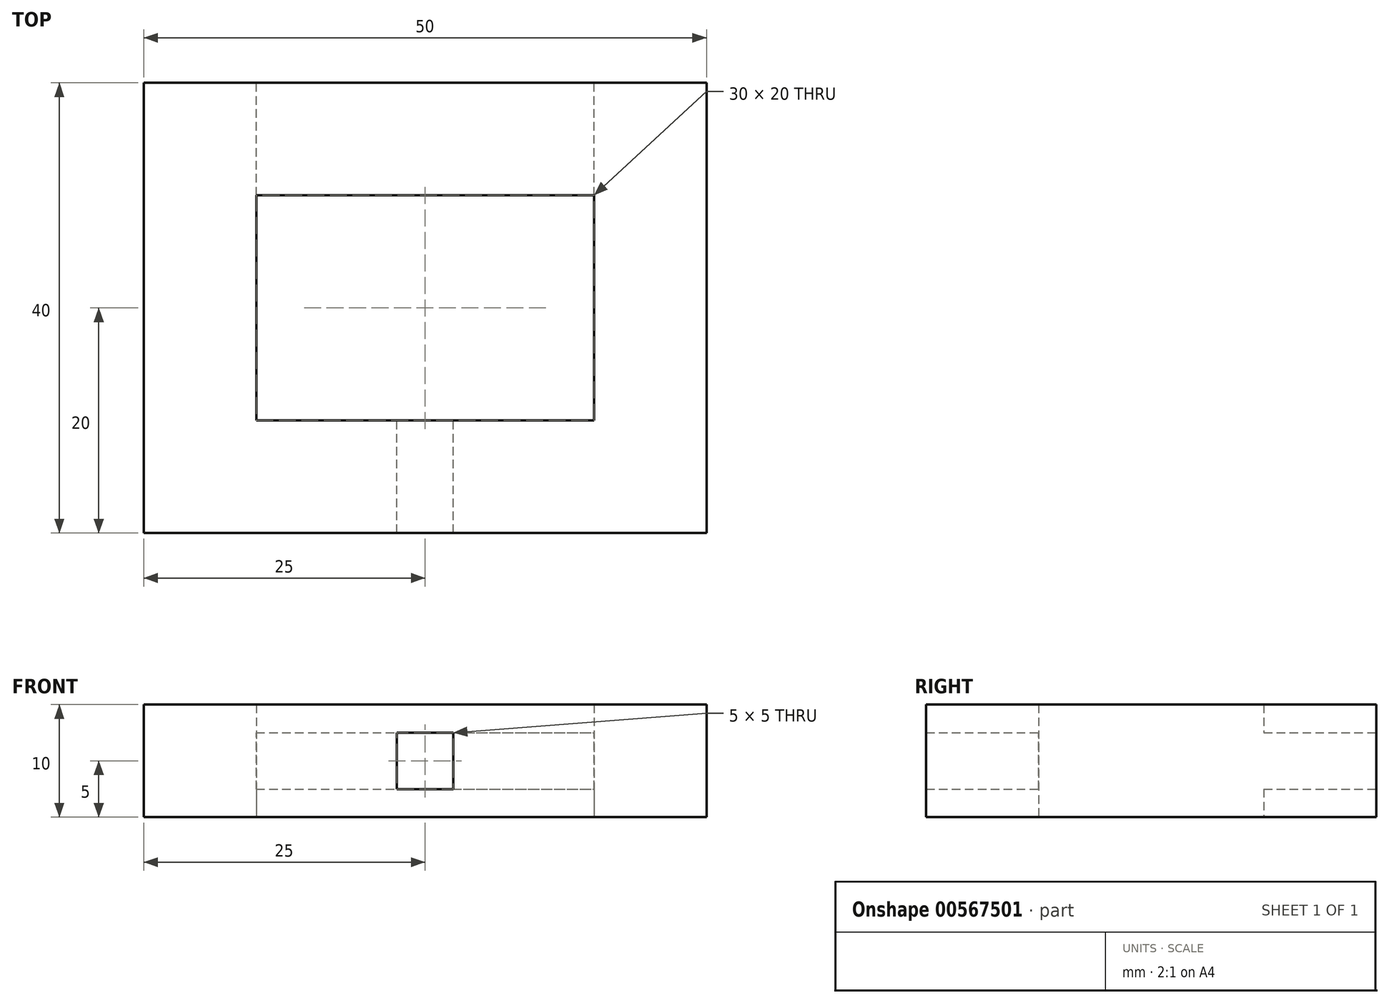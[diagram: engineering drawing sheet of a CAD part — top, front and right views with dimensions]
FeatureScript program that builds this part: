
annotation { "Feature Type Name" : "Feature", "Feature Type Description" : "" }
export const myFeature = defineFeature(function(context is Context, id is Id, definition is map)
    precondition{}
    {
        {
            var Q0;
            Q0=qCreatedBy(makeId("Top.planeOp"),FACE);
            var sketch = newSketch(context, id + "F0", { "sketchPlane" : qUnion([Q0])});
            skLineSegment(sketch, "E0.bottom", {"start": v(-25, 20) * mm, "end": v(25, 20) * mm});
            skLineSegment(sketch, "E0.top", {"start": v(-25, -20) * mm, "end": v(25, -20) * mm});
            skLineSegment(sketch, "E0.left", {"start": v(-25, 20) * mm, "end": v(-25, -20) * mm});
            skLineSegment(sketch, "E0.right", {"start": v(25, 20) * mm, "end": v(25, -20) * mm});
            skPoint(sketch, "E0.middle", {"position": v(0, 0) * mm});
            skLineSegment(sketch, "E1.0", {"start": v(15, 10) * mm, "end": v(15, -10) * mm});
            skLineSegment(sketch, "E1.1", {"start": v(-15, 10) * mm, "end": v(15, 10) * mm});
            skLineSegment(sketch, "E1.2", {"start": v(-15, 10) * mm, "end": v(-15, -10) * mm});
            skLineSegment(sketch, "E1.3", {"start": v(-15, -10) * mm, "end": v(15, -10) * mm});
            skSolve(sketch);
        }
        {
            var Q0;
            Q0=makeQuery(id+"F0.imprint","IMPRINT",FACE,{"disambiguationData":[TD([[makeQuery(id+"F0.imprint","IMPRINT",EDGE,{"derivedFrom":sQuery(id+"F0.wireOp",EDGE,"E0.bottom")}),-1.0]])]});
            extrude(context, id + "F1", {"entities" : qUnion([Q0]), "depth" : 10 * mm, "offsetDistance" : 25 * mm});
        }
        {
            var Q0;
            Q0=makeQuery(id+"F1.opExtrude","SWEPT_FACE",FACE,{"disambiguationData":[OSD([sQuery(id+"F0.wireOp",EDGE,"E0.bottom")])]});
            var sketch = newSketch(context, id + "F2", { "sketchPlane" : qUnion([Q0])});
            skLineSegment(sketch, "E2", {"start": v(-25, 5) * mm, "end": v(25, 5) * mm, "construction": true});
            skLineSegment(sketch, "E3", {"start": v(0, 10) * mm, "end": v(0, 0) * mm, "construction": true});
            skLineSegment(sketch, "E4.bottom", {"start": v(15, 2.5) * mm, "end": v(-15, 2.5) * mm});
            skLineSegment(sketch, "E4.top", {"start": v(15, 7.5) * mm, "end": v(-15, 7.5) * mm});
            skLineSegment(sketch, "E4.left", {"start": v(15, 2.5) * mm, "end": v(15, 7.5) * mm});
            skLineSegment(sketch, "E4.right", {"start": v(-15, 2.5) * mm, "end": v(-15, 7.5) * mm});
            skPoint(sketch, "E4.middle", {"position": v(0, 5) * mm});
            skSolve(sketch);
        }
        {
            var Q0;
            Q0=makeQuery(id+"F2.imprint","IMPRINT",FACE,{"disambiguationData":[TD([[makeQuery(id+"F2.imprint","IMPRINT",EDGE,{"derivedFrom":sQuery(id+"F2.wireOp",EDGE,"E4.bottom")}),-1.0]])]});
            extrude(context, id + "F3", {"entities" : qUnion([Q0]), "operationType" : NewBodyOperationType.REMOVE, "oppositeDirection" : true, "depth" : 25 * mm, "offsetDistance" : 25 * mm});
        }
        {
            var Q0;
            Q0=makeQuery(id+"F1.opExtrude","SWEPT_FACE",FACE,{"disambiguationData":[OSD([sQuery(id+"F0.wireOp",EDGE,"E1.3")])]});
            var sketch = newSketch(context, id + "F4", { "sketchPlane" : qUnion([Q0])});
            skLineSegment(sketch, "E5", {"start": v(-15, 5) * mm, "end": v(15, 5) * mm, "construction": true});
            skLineSegment(sketch, "E6", {"start": v(0, 7.69) * mm, "end": v(0, 2.87) * mm, "construction": true});
            skPoint(sketch, "E6.endSnap0", {"position": v(0, 5) * mm});
            skLineSegment(sketch, "E7.bottom", {"start": v(2.5, 2.5) * mm, "end": v(-2.5, 2.5) * mm});
            skLineSegment(sketch, "E7.top", {"start": v(2.5, 7.5) * mm, "end": v(-2.5, 7.5) * mm});
            skLineSegment(sketch, "E7.left", {"start": v(2.5, 2.5) * mm, "end": v(2.5, 7.5) * mm});
            skLineSegment(sketch, "E7.right", {"start": v(-2.5, 2.5) * mm, "end": v(-2.5, 7.5) * mm});
            skSolve(sketch);
        }
        {
            var Q0;
            Q0=makeQuery(id+"F4.imprint","IMPRINT",FACE,{"disambiguationData":[TD([[makeQuery(id+"F4.imprint","IMPRINT",EDGE,{"derivedFrom":sQuery(id+"F4.wireOp",EDGE,"E7.bottom")}),-1.0]])]});
            extrude(context, id + "F5", {"entities" : qUnion([Q0]), "operationType" : NewBodyOperationType.REMOVE, "endBound" : BoundingType.UP_TO_NEXT, "oppositeDirection" : true, "depth" : 25 * mm, "offsetDistance" : 25 * mm});
        }
    });
